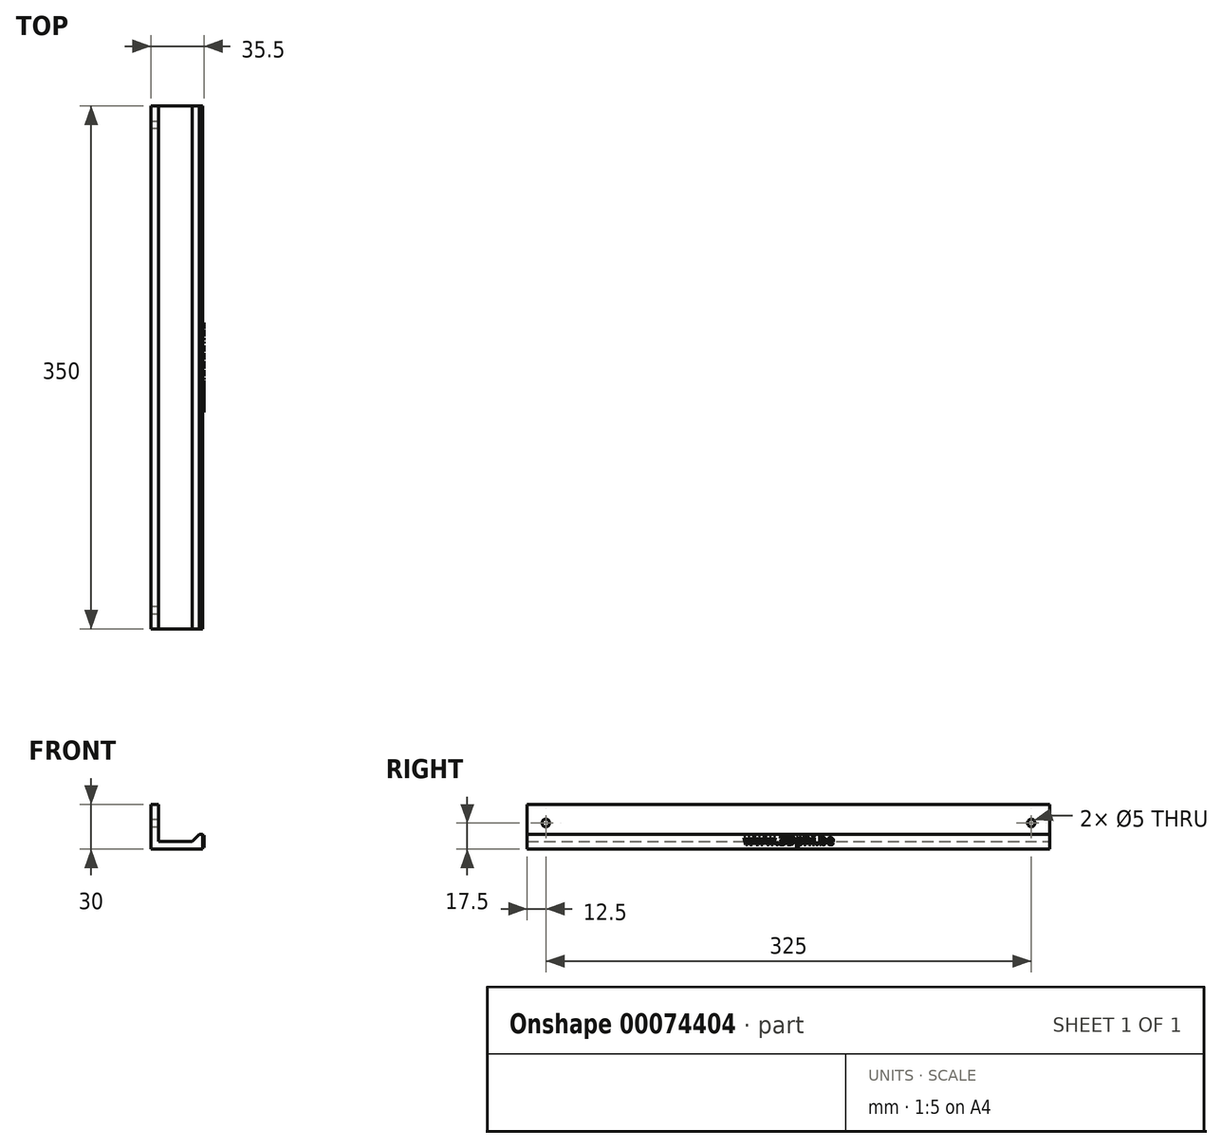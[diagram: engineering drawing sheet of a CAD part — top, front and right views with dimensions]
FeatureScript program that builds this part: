
annotation { "Feature Type Name" : "Feature", "Feature Type Description" : "" }
export const myFeature = defineFeature(function(context is Context, id is Id, definition is map)
    precondition{}
    {
        {
            var Q0;
            Q0=qCreatedBy(makeId("Front.planeOp"),FACE);
            var sketch = newSketch(context, id + "F0", { "sketchPlane" : qUnion([Q0])});
            skLineSegment(sketch, "E0", {"start": v(0, 0) * mm, "end": v(34.5, 0) * mm});
            skLineSegment(sketch, "E1", {"start": v(34.5, 0) * mm, "end": v(34.5, 10) * mm});
            skLineSegment(sketch, "E2", {"start": v(34.5, 10) * mm, "end": v(32.5, 10) * mm});
            skLineSegment(sketch, "E3", {"start": v(32.5, 10) * mm, "end": v(32.5, 5) * mm});
            skLineSegment(sketch, "E4", {"start": v(32.5, 5) * mm, "end": v(5, 5) * mm});
            skLineSegment(sketch, "E5", {"start": v(5, 5) * mm, "end": v(5, 30) * mm});
            skLineSegment(sketch, "E6", {"start": v(5, 30) * mm, "end": v(0, 30) * mm});
            skLineSegment(sketch, "E7", {"start": v(0, 30) * mm, "end": v(0, 0) * mm});
            skSolve(sketch);
        }
        {
            var Q0;
            Q0 = qSketchRegion(id + "F0", true);
            extrude(context, id + "F1", {"entities" : qUnion([Q0]), "depth" : 350 * mm});
        }
        {
            var Q0;
            Q0=makeQuery(id+"F1.opExtrude","SWEPT_FACE",FACE,{"disambiguationData":[OSD([sQuery(id+"F0.wireOp",EDGE,"E5")])]});
            var sketch = newSketch(context, id + "F2", { "sketchPlane" : qUnion([Q0])});
            skLineSegment(sketch, "E8", {"start": v(-350, 17.5) * mm, "end": v(0, 17.5) * mm, "construction": true});
            skLineSegment(sketch, "E9", {"start": v(-175, 30) * mm, "end": v(-175, 17.5) * mm, "construction": true});
            skCircle(sketch, "E10", {"center": v(-337.5, 17.5) * mm, "radius": 2.5 * mm});
            skCircle(sketch, "E11.MirrorC", {"center": v(-12.5, 17.5) * mm, "radius": 2.5 * mm});
            skSolve(sketch);
        }
        {
            var Q0;
            Q0 = qSketchRegion(id + "F2", true);
            extrude(context, id + "F3", {"entities" : qUnion([Q0]), "operationType" : NewBodyOperationType.REMOVE, "oppositeDirection" : true, "depth" : 25 * mm});
        }
        {
            var Q0;
            Q0=makeQuery(id+"F1.opExtrude","SWEPT_FACE",FACE,{"disambiguationData":[OSD([sQuery(id+"F0.wireOp",EDGE,"E1")])]});
            var sketch = newSketch(context, id + "F4", { "sketchPlane" : qUnion([Q0])});
            skLineSegment(sketch, "E12", {"start": v(-175, 10) * mm, "end": v(-175, 0) * mm, "construction": true});
            skText(sketch, "E13", { "text": "www.3Dphi.be", "fontName": "OpenSans-Bold.ttf"});
            const initialGuessF4  = {"E13": [-0.2051, 0.003, 1, 0, 0.006]};
            skSetInitialGuess(sketch, initialGuessF4);
            skSolve(sketch);
        }
        {
            var Q0;
            Q0 = qSketchRegion(id + "F4", true);
            extrude(context, id + "F5", {"entities" : qUnion([Q0]), "operationType" : NewBodyOperationType.ADD, "depth" : 1 * mm});
        }
        {
            var Q0;
            Q0=makeQuery(id+"F1.opExtrude","SWEPT_EDGE",EDGE,{"disambiguationData":[OSD([sQuery(id+"F0.wireOp",EDGE,"E3"),sQuery(id+"F0.wireOp",EDGE,"E4")])]});
            chamfer(context, id + "F6", {"entities" : qUnion([Q0]), "width" : 5 * mm, "tangentPropagation" : true});
        }
    });
